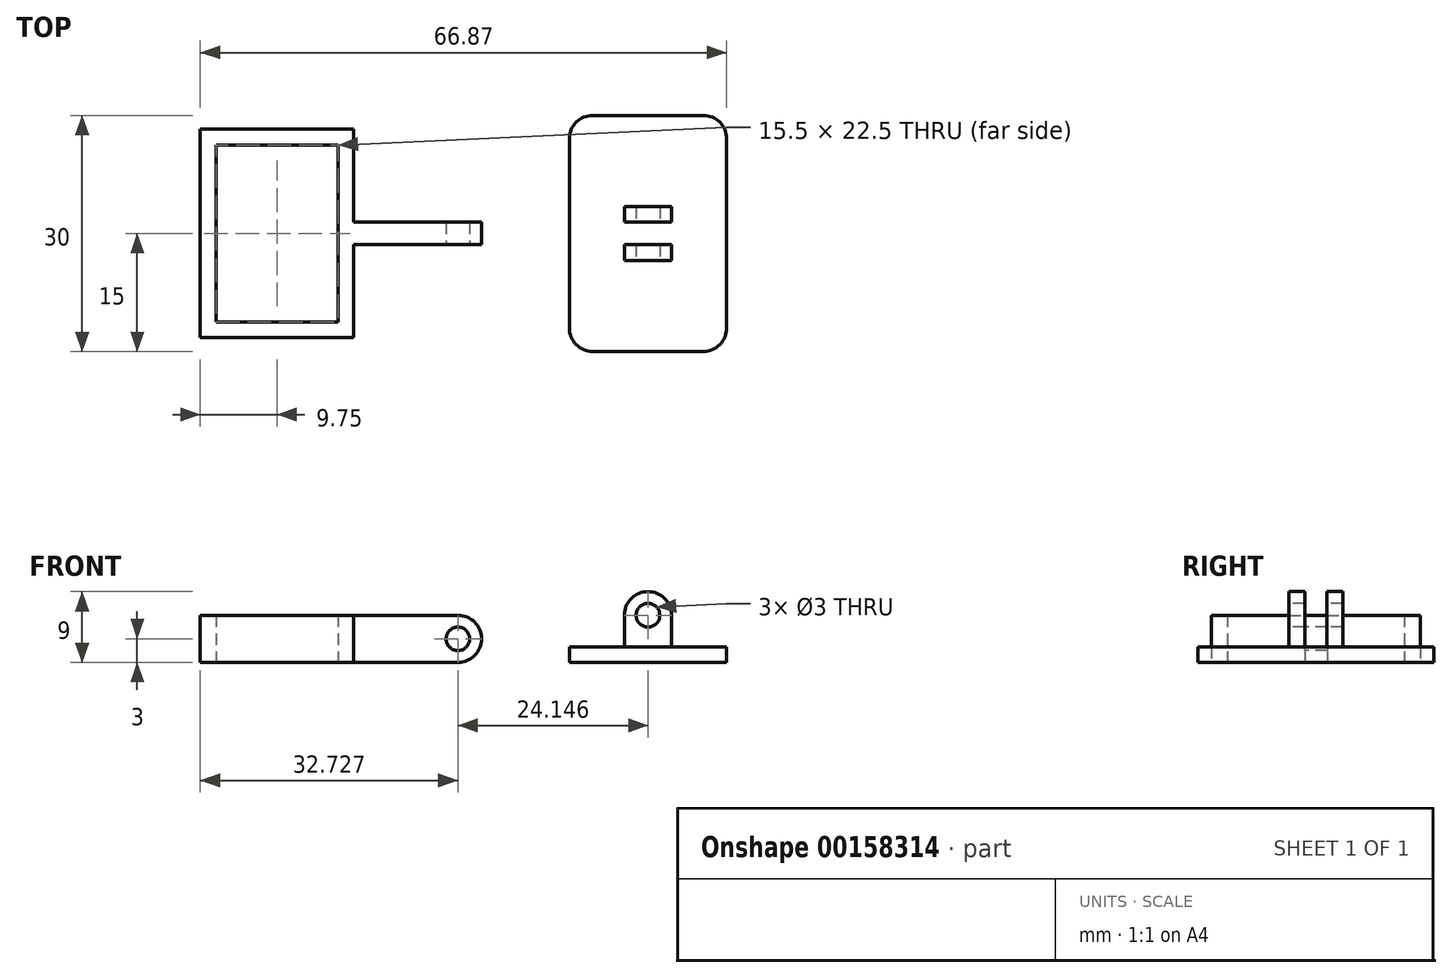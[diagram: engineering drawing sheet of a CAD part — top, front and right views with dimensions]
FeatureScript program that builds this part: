
annotation { "Feature Type Name" : "Feature", "Feature Type Description" : "" }
export const myFeature = defineFeature(function(context is Context, id is Id, definition is map)
    precondition{}
    {
        {
            var Q0;
            Q0=qCreatedBy(makeId("Top.planeOp"),FACE);
            var sketch = newSketch(context, id + "F0", { "sketchPlane" : qUnion([Q0])});
            skLineSegment(sketch, "E0.bottom", {"start": v(7.75, -11.25) * mm, "end": v(-7.75, -11.25) * mm});
            skLineSegment(sketch, "E0.top", {"start": v(7.75, 11.25) * mm, "end": v(-7.75, 11.25) * mm});
            skLineSegment(sketch, "E0.left", {"start": v(7.75, -11.25) * mm, "end": v(7.75, 11.25) * mm});
            skLineSegment(sketch, "E0.right", {"start": v(-7.75, -11.25) * mm, "end": v(-7.75, 11.25) * mm});
            skPoint(sketch, "E0.middle", {"position": v(0, 0) * mm});
            skLineSegment(sketch, "E1.0", {"start": v(9.75, -13.25) * mm, "end": v(-9.75, -13.25) * mm});
            skLineSegment(sketch, "E1.1", {"start": v(9.75, -13.25) * mm, "end": v(9.75, 13.25) * mm});
            skLineSegment(sketch, "E1.2", {"start": v(9.75, 13.25) * mm, "end": v(-9.75, 13.25) * mm});
            skLineSegment(sketch, "E1.3", {"start": v(-9.75, -13.25) * mm, "end": v(-9.75, 13.25) * mm});
            skLineSegment(sketch, "E2.bottom", {"start": v(9.75, -1.43) * mm, "end": v(25.98, -1.43) * mm});
            skLineSegment(sketch, "E2.top", {"start": v(9.75, 1.43) * mm, "end": v(25.98, 1.43) * mm});
            skLineSegment(sketch, "E2.left", {"start": v(9.75, -1.43) * mm, "end": v(9.75, 1.43) * mm});
            skLineSegment(sketch, "E2.right", {"start": v(25.98, -1.43) * mm, "end": v(25.98, 1.43) * mm});
            skPoint(sketch, "E2.middle", {"position": v(17.86, 0) * mm});
            skSolve(sketch);
        }
        {
            var Q0;
            Q0=makeQuery(id+"F0.imprint","IMPRINT",FACE,{"disambiguationData":[TD([[makeQuery(id+"F0.imprint","IMPRINT",EDGE,{"derivedFrom":sQuery(id+"F0.wireOp",EDGE,"E0.bottom")}),1.0]])]});
            var Q1;
            {var subQ2=sQuery(id+"F0.wireOp",EDGE,"E2.bottom");Q1=makeQuery(id+"F0.imprint","IMPRINT",FACE,{"disambiguationData":[TD([[makeQuery(id+"F0.imprint","IMPRINT",EDGE,{"derivedFrom":subQ2}),1.0]])]});}
            extrude(context, id + "F1", {"entities" : qUnion([Q0, Q1]), "depth" : 6 * mm, "offsetDistance" : 25 * mm});
        }
        {
            var Q0;
            Q0=makeQuery(id+"F1.opExtrude","SWEPT_FACE",FACE,{"disambiguationData":[OSD([sQuery(id+"F0.wireOp",EDGE,"E2.bottom")])]});
            var sketch = newSketch(context, id + "F2", { "sketchPlane" : qUnion([Q0])});
            skCircle(sketch, "E3", {"center": v(22.98, 3) * mm, "radius": 1.5 * mm});
            skPoint(sketch, "E4", {"position": v(9.75, 3) * mm});
            skSolve(sketch);
        }
        {
            var Q0;
            Q0=makeQuery(id+"F2.imprint","IMPRINT",FACE,{"disambiguationData":[TD([[makeQuery(id+"F2.imprint","IMPRINT",EDGE,{"derivedFrom":sQuery(id+"F2.wireOp",EDGE,"E3")}),1.0]])]});
            extrude(context, id + "F3", {"entities" : qUnion([Q0]), "operationType" : NewBodyOperationType.REMOVE, "oppositeDirection" : true, "depth" : 25 * mm, "offsetDistance" : 25 * mm});
        }
        {
            var Q0;
            Q0=qCreatedBy(makeId("Top.planeOp"),FACE);
            var sketch = newSketch(context, id + "F4", { "sketchPlane" : qUnion([Q0])});
            skLineSegment(sketch, "E5.bottom", {"start": v(57.12, -15) * mm, "end": v(37.12, -15) * mm});
            skLineSegment(sketch, "E5.top", {"start": v(57.12, 15) * mm, "end": v(37.12, 15) * mm});
            skLineSegment(sketch, "E5.left", {"start": v(57.12, -15) * mm, "end": v(57.12, 15) * mm});
            skLineSegment(sketch, "E5.right", {"start": v(37.12, -15) * mm, "end": v(37.12, 15) * mm});
            skPoint(sketch, "E5.middle", {"position": v(47.12, 0) * mm});
            skLineSegment(sketch, "E6.bottom", {"start": v(50.12, -3.42) * mm, "end": v(44.12, -3.42) * mm});
            skLineSegment(sketch, "E6.top", {"start": v(50.12, -1.42) * mm, "end": v(44.12, -1.42) * mm});
            skLineSegment(sketch, "E6.left", {"start": v(50.12, -3.42) * mm, "end": v(50.12, -1.42) * mm});
            skLineSegment(sketch, "E6.right", {"start": v(44.12, -3.42) * mm, "end": v(44.12, -1.42) * mm});
            skPoint(sketch, "E6.middle", {"position": v(47.12, -2.42) * mm});
            skLineSegment(sketch, "E7", {"start": v(22.8, -1.46) * mm, "end": v(79.65, -1.46) * mm, "construction": true});
            skLineSegment(sketch, "E8.MirrorCS", {"start": v(50.12, 1.42) * mm, "end": v(44.12, 1.42) * mm});
            skLineSegment(sketch, "E9.MirrorCS", {"start": v(50.12, 3.42) * mm, "end": v(44.12, 3.42) * mm});
            skLineSegment(sketch, "E10.MirrorCS", {"start": v(44.12, 3.42) * mm, "end": v(44.12, 1.42) * mm});
            skLineSegment(sketch, "E11.MirrorCS", {"start": v(50.12, 3.42) * mm, "end": v(50.12, 1.42) * mm});
            skLineSegment(sketch, "E12.MirrorCS", {"start": v(22.8, 1.46) * mm, "end": v(79.65, 1.46) * mm, "construction": true});
            skPoint(sketch, "E13.MirrorP", {"position": v(47.12, 2.42) * mm});
            skSolve(sketch);
        }
        {
            var Q0;
            Q0=makeQuery(id+"F4.imprint","IMPRINT",FACE,{"disambiguationData":[TD([[makeQuery(id+"F4.imprint","IMPRINT",EDGE,{"derivedFrom":sQuery(id+"F4.wireOp",EDGE,"E8.MirrorCS")}),-1.0]])]});
            var Q1;
            Q1=makeQuery(id+"F4.imprint","IMPRINT",FACE,{"disambiguationData":[TD([[makeQuery(id+"F4.imprint","IMPRINT",EDGE,{"derivedFrom":sQuery(id+"F4.wireOp",EDGE,"E6.bottom")}),-1.0]])]});
            var Q2;
            Q2=makeQuery(id+"F4.imprint","IMPRINT",FACE,{"disambiguationData":[TD([[makeQuery(id+"F4.imprint","IMPRINT",EDGE,{"derivedFrom":sQuery(id+"F4.wireOp",EDGE,"E5.bottom")}),-1.0]])]});
            extrude(context, id + "F5", {"entities" : qUnion([Q0, Q1, Q2]), "depth" : 2 * mm, "offsetDistance" : 25 * mm});
        }
        {
            var Q0;
            Q0=makeQuery(id+"F4.imprint","IMPRINT",FACE,{"disambiguationData":[TD([[makeQuery(id+"F4.imprint","IMPRINT",EDGE,{"derivedFrom":sQuery(id+"F4.wireOp",EDGE,"E8.MirrorCS")}),-1.0]])]});
            var Q1;
            Q1=makeQuery(id+"F4.imprint","IMPRINT",FACE,{"disambiguationData":[TD([[makeQuery(id+"F4.imprint","IMPRINT",EDGE,{"derivedFrom":sQuery(id+"F4.wireOp",EDGE,"E6.bottom")}),-1.0]])]});
            extrude(context, id + "F6", {"entities" : qUnion([Q0, Q1]), "operationType" : NewBodyOperationType.ADD, "depth" : 9 * mm, "offsetDistance" : 25 * mm});
        }
        {
            var Q0;
            Q0=makeQuery(id+"F1.opExtrude","CAP_EDGE",EDGE,{"disambiguationData":[OSD([sQuery(id+"F0.wireOp",EDGE,"E2.right")])],"isStart":true});
            var Q1;
            Q1=makeQuery(id+"F1.opExtrude","CAP_EDGE",EDGE,{"disambiguationData":[OSD([sQuery(id+"F0.wireOp",EDGE,"E2.right")])],"isStart":false});
            var Q2;
            Q2=makeQuery(id+"F6.opExtrude","CAP_EDGE",EDGE,{"disambiguationData":[OSD([sQuery(id+"F4.wireOp",EDGE,"E10.MirrorCS")])],"isStart":false});
            var Q3;
            Q3=makeQuery(id+"F6.opExtrude","CAP_EDGE",EDGE,{"disambiguationData":[OSD([sQuery(id+"F4.wireOp",EDGE,"E6.right")])],"isStart":false});
            var Q4;
            Q4=makeQuery(id+"F6.opExtrude","CAP_EDGE",EDGE,{"disambiguationData":[OSD([sQuery(id+"F4.wireOp",EDGE,"E11.MirrorCS")])],"isStart":false});
            var Q5;
            Q5=makeQuery(id+"F6.opExtrude","CAP_EDGE",EDGE,{"disambiguationData":[OSD([sQuery(id+"F4.wireOp",EDGE,"E6.left")])],"isStart":false});
            var Q6;
            Q6=makeQuery(id+"F5.opExtrude","SWEPT_EDGE",EDGE,{"disambiguationData":[OSD([sQuery(id+"F4.wireOp",EDGE,"E5.bottom"),sQuery(id+"F4.wireOp",EDGE,"E5.right")])]});
            var Q7;
            Q7=makeQuery(id+"F5.opExtrude","SWEPT_EDGE",EDGE,{"disambiguationData":[OSD([sQuery(id+"F4.wireOp",EDGE,"E5.bottom"),sQuery(id+"F4.wireOp",EDGE,"E5.left")])]});
            var Q8;
            Q8=makeQuery(id+"F5.opExtrude","SWEPT_EDGE",EDGE,{"disambiguationData":[OSD([sQuery(id+"F4.wireOp",EDGE,"E5.top"),sQuery(id+"F4.wireOp",EDGE,"E5.left")])]});
            var Q9;
            Q9=makeQuery(id+"F5.opExtrude","SWEPT_EDGE",EDGE,{"disambiguationData":[OSD([sQuery(id+"F4.wireOp",EDGE,"E5.top"),sQuery(id+"F4.wireOp",EDGE,"E5.right")])]});
            fillet(context, id + "F7", {"entities" : qUnion([Q0, Q1, Q2, Q3, Q4, Q5, Q6, Q7, Q8, Q9]), "radius" : 3 * mm, "tangentPropagation" : true, "allowEdgeOverflow" : false});
        }
        {
            var Q0;
            Q0=makeQuery(id+"F6.opExtrude","SWEPT_FACE",FACE,{"disambiguationData":[OSD([sQuery(id+"F4.wireOp",EDGE,"E6.bottom")])]});
            var sketch = newSketch(context, id + "F8", { "sketchPlane" : qUnion([Q0])});
            skCircle(sketch, "E14", {"center": v(47.12, 6) * mm, "radius": 1.5 * mm});
            skSolve(sketch);
        }
        {
            var Q0;
            Q0=makeQuery(id+"F8.imprint","IMPRINT",FACE,{"disambiguationData":[TD([[makeQuery(id+"F8.imprint","IMPRINT",EDGE,{"derivedFrom":sQuery(id+"F8.wireOp",EDGE,"E14")}),1.0]])]});
            extrude(context, id + "F9", {"entities" : qUnion([Q0]), "operationType" : NewBodyOperationType.REMOVE, "oppositeDirection" : true, "depth" : 25 * mm, "offsetDistance" : 25 * mm});
        }
    });
